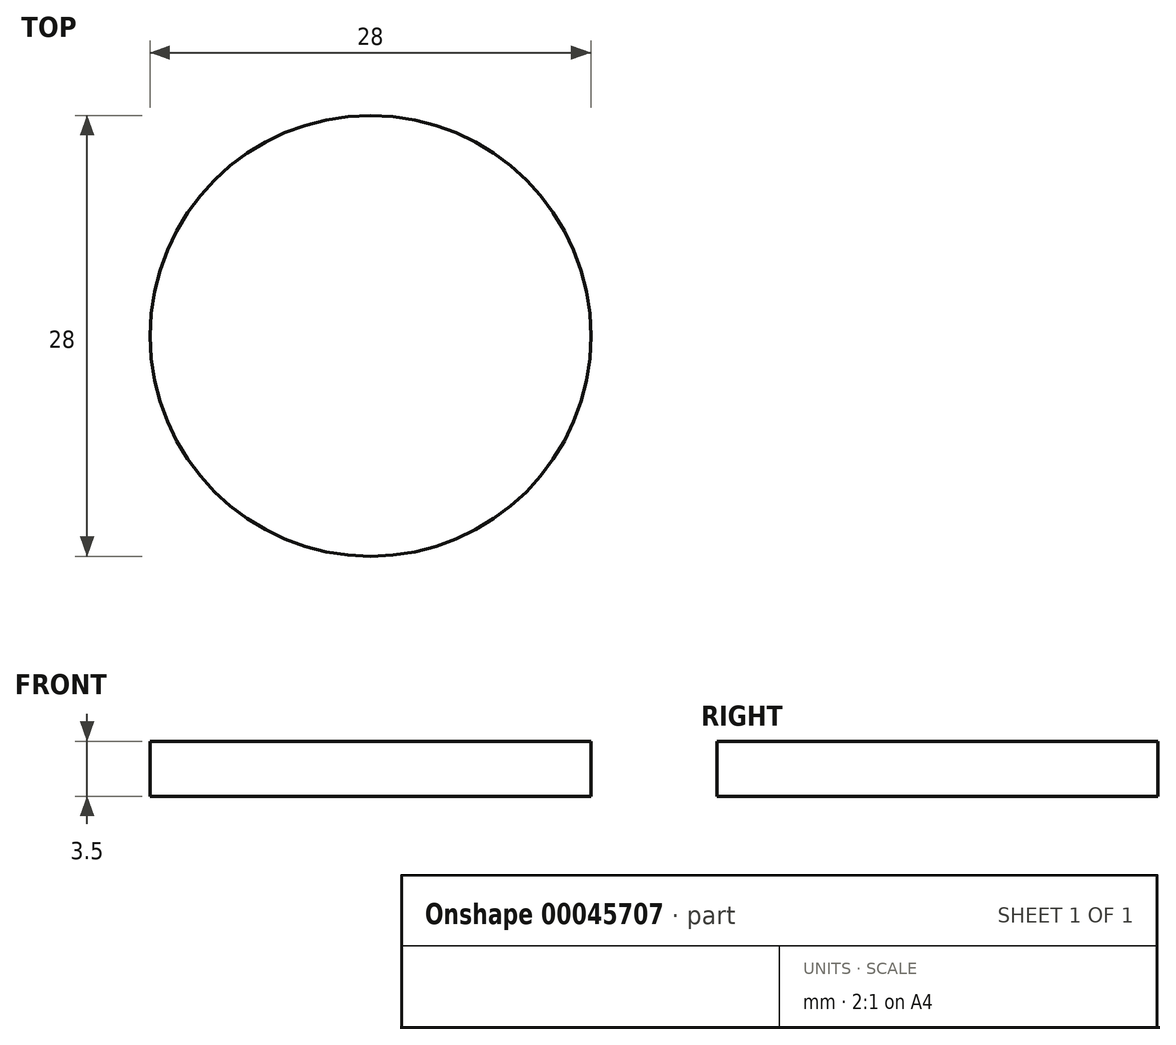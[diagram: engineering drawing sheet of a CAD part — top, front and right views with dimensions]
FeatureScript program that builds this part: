
annotation { "Feature Type Name" : "Feature", "Feature Type Description" : "" }
export const myFeature = defineFeature(function(context is Context, id is Id, definition is map)
    precondition{}
    {
        {
            var Q0;
            Q0=qCreatedBy(makeId("Top.planeOp"),FACE);
            var sketch = newSketch(context, id + "F0", { "sketchPlane" : qUnion([Q0])});
            skCircle(sketch, "E0", {"center": v(0, 0) * mm, "radius": 14 * mm});
            skSolve(sketch);
        }
        {
            var Q0;
            Q0=makeQuery(id+"F0.imprint","IMPRINT",FACE,{"disambiguationData":[TD([[makeQuery(id+"F0.imprint","IMPRINT",EDGE,{"derivedFrom":sQuery(id+"F0.wireOp",EDGE,"E0")}),1.0]])]});
            extrude(context, id + "F1", {"entities" : qUnion([Q0]), "depth" : 3.5 * mm});
        }
    });
